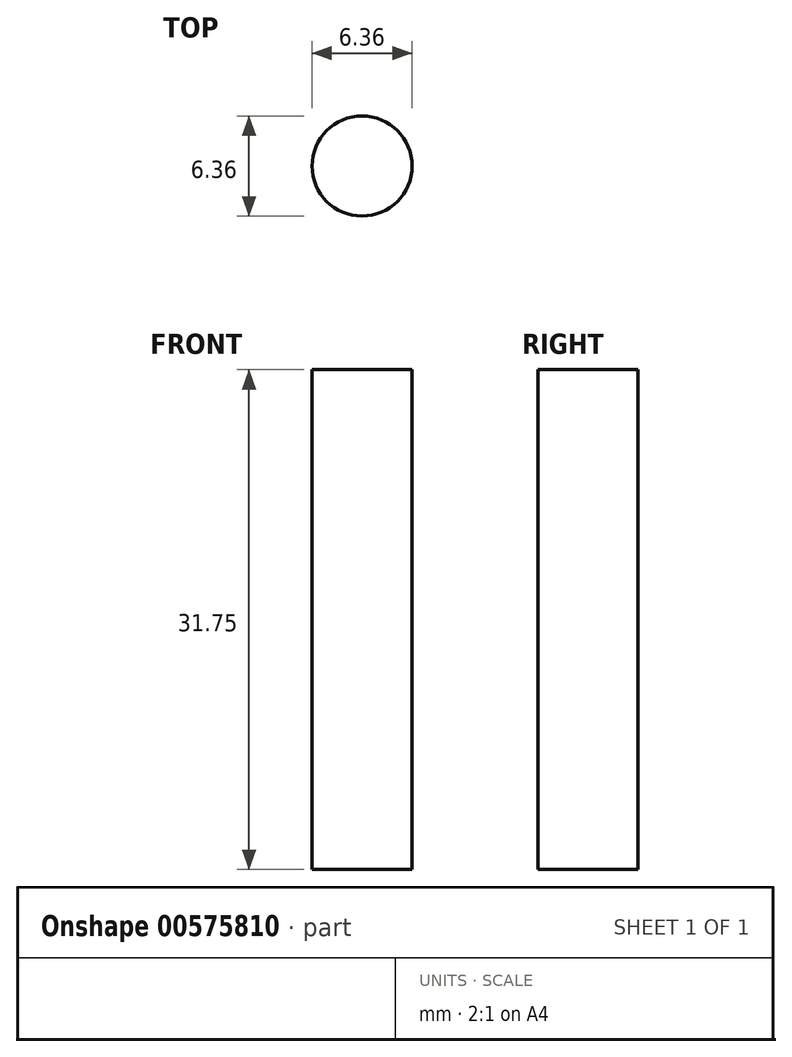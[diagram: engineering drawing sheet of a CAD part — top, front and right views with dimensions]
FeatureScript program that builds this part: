
annotation { "Feature Type Name" : "Feature", "Feature Type Description" : "" }
export const myFeature = defineFeature(function(context is Context, id is Id, definition is map)
    precondition{}
    {
        {
            var Q0;
            Q0=qCreatedBy(makeId("Top.planeOp"),FACE);
            var sketch = newSketch(context, id + "F0", { "sketchPlane" : qUnion([Q0])});
            skCircle(sketch, "E0", {"center": v(0, 0) * mm, "radius": 3.17 * mm});
            skSolve(sketch);
        }
        {
            var Q0;
            Q0 = qSketchRegion(id + "F0", true);
            extrude(context, id + "F1", {"entities" : qUnion([Q0]), "depth" : 31.75 * mm, "offsetDistance" : 25.4 * mm});
        }
    });
